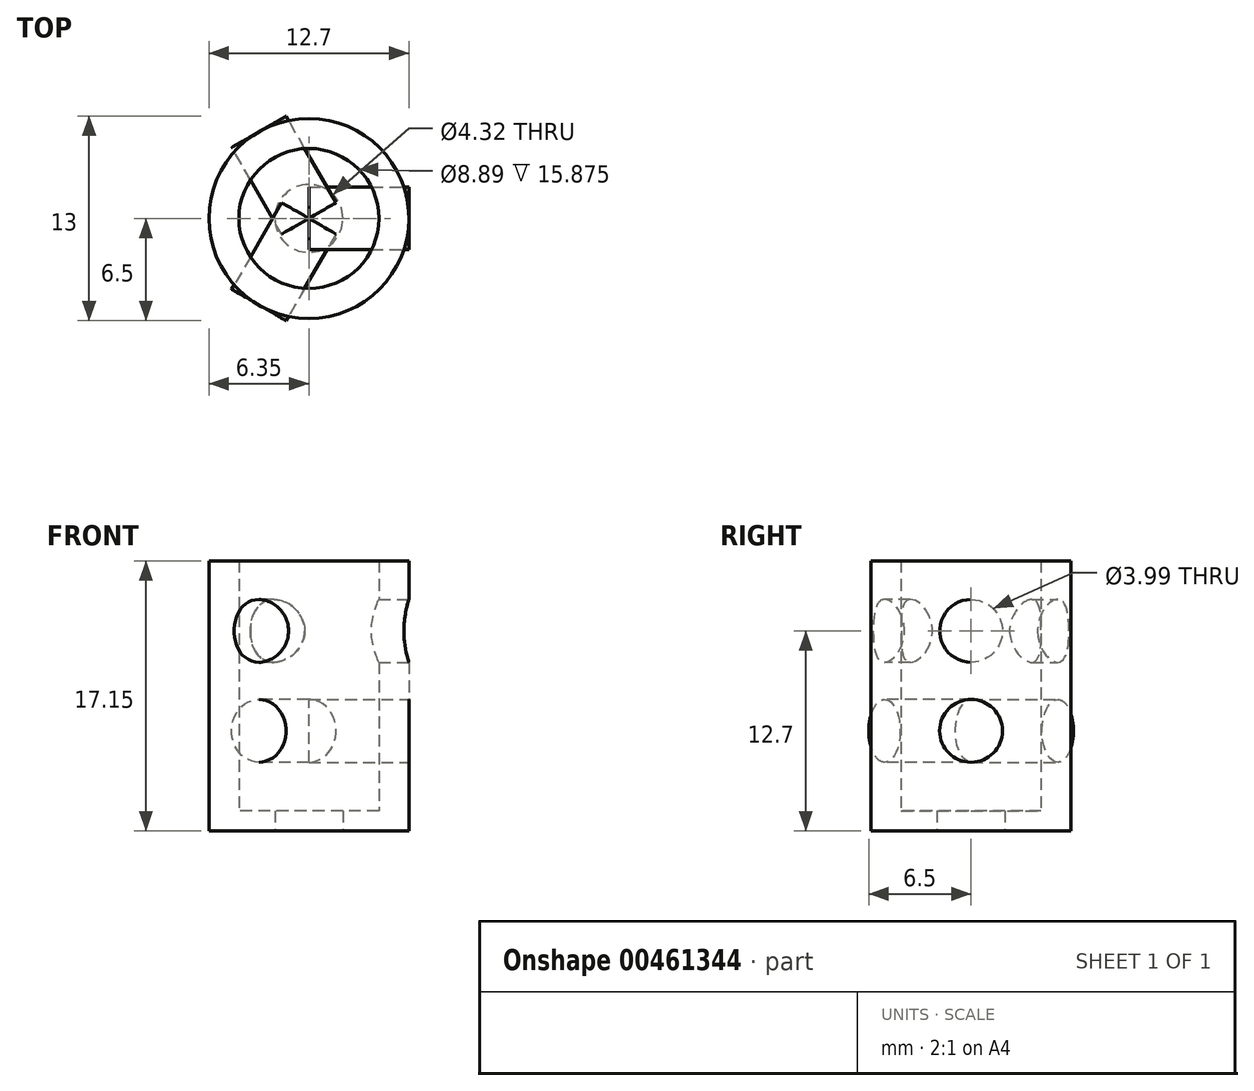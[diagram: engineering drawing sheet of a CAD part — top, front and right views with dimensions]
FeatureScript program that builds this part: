
annotation { "Feature Type Name" : "Feature", "Feature Type Description" : "" }
export const myFeature = defineFeature(function(context is Context, id is Id, definition is map)
    precondition{}
    {
        {
            var Q0;
            Q0=qCreatedBy(makeId("Top.planeOp"),FACE);
            var sketch = newSketch(context, id + "F0", { "sketchPlane" : qUnion([Q0])});
            skCircle(sketch, "E0", {"center": v(0, 0) * mm, "radius": 6.35 * mm});
            skCircle(sketch, "E1", {"center": v(0, 0) * mm, "radius": 2.16 * mm});
            skSolve(sketch);
        }
        {
            var Q0;
            Q0=makeQuery(id+"F0.imprint","IMPRINT",FACE,{"disambiguationData":[TD([[makeQuery(id+"F0.imprint","IMPRINT",EDGE,{"derivedFrom":sQuery(id+"F0.wireOp",EDGE,"E0")}),1.0]])]});
            extrude(context, id + "F1", {"entities" : qUnion([Q0]), "depth" : 1.27 * mm});
        }
        {
            var Q0;
            Q0=makeQuery(id+"F1.opExtrude","CAP_FACE",FACE,{"disambiguationData":[OSD([sQuery(id+"F0.wireOp",EDGE,"E0"),sQuery(id+"F0.wireOp",EDGE,"E1")])],"isStart":false});
            var sketch = newSketch(context, id + "F2", { "sketchPlane" : qUnion([Q0])});
            skCircle(sketch, "E2", {"center": v(0, 0) * mm, "radius": 6.35 * mm});
            skCircle(sketch, "E3", {"center": v(0, 0) * mm, "radius": 4.45 * mm});
            skSolve(sketch);
        }
        {
            var Q0;
            Q0=makeQuery(id+"F2.imprint","IMPRINT",FACE,{"disambiguationData":[TD([[makeQuery(id+"F2.imprint","IMPRINT",EDGE,{"derivedFrom":sQuery(id+"F2.wireOp",EDGE,"E2")}),1.0]])]});
            extrude(context, id + "F3", {"entities" : qUnion([Q0]), "operationType" : NewBodyOperationType.ADD, "depth" : 15.88 * mm, "offsetDistance" : 25.4 * mm});
        }
        {
            var Q0;
            Q0=qCreatedBy(makeId("Right.planeOp"),FACE);
            cPlane(context, id + "F4", {"entities" : qUnion([Q0]), "cplaneType" : CPlaneType.OFFSET, "offset" : 6.35 * mm, "width" : 152.4 * mm, "height" : 152.4 * mm});
        }
        {
            var Q0;
            Q0=qCreatedBy(id+"F4.planeOp",FACE);
            var sketch = newSketch(context, id + "F5", { "sketchPlane" : qUnion([Q0])});
            skCircle(sketch, "E4", {"center": v(0, 6.35) * mm, "radius": 2 * mm});
            skCircle(sketch, "E5", {"center": v(0, 12.7) * mm, "radius": 2 * mm});
            skSolve(sketch);
        }
        {
            var Q0;
            Q0 = qSketchRegion(id + "F5", true);
            extrude(context, id + "F6", {"entities" : qUnion([Q0]), "oppositeDirection" : true, "depth" : 6.35 * mm, "offsetDistance" : 25.4 * mm});
        }
        {
            var Q0;
            Q0=makeQuery(id+"F6.opExtrude","SWEPT_BODY",BODY,{"disambiguationData":[OSD([sQuery(id+"F5.wireOp",EDGE,"E4")])]});
            var Q1;
            Q1=makeQuery(id+"F6.opExtrude","SWEPT_BODY",BODY,{"disambiguationData":[OSD([sQuery(id+"F5.wireOp",EDGE,"E5")])]});
            var Q2;
            Q2=makeQuery(id+"F3.opExtrude","CAP_EDGE",EDGE,{"disambiguationData":[OSD([sQuery(id+"F2.wireOp",EDGE,"E3")])],"isStart":false});
            circularPattern(context, id + "F7", {"entities" : qUnion([Q0, Q1]), "axis" : qUnion([Q2]), "angle" : 360 * degree, "instanceCount" : 3, "equalSpace" : true});
        }
        {
            var Q0;
            Q0=makeQuery(id+"F6.opExtrude","CAP_FACE",FACE,{"disambiguationData":[OSD([sQuery(id+"F5.wireOp",EDGE,"E4")])],"isStart":true});
            var sketch = newSketch(context, id + "F8", { "sketchPlane" : qUnion([Q0])});
            skSolve(sketch);
        }
        {
            var Q0;
            Q0=makeQuery(id+"F8.imprint","IMPRINT",FACE,{"disambiguationData":[TD([[makeQuery(id+"F8.imprint","IMPRINT",EDGE,{"derivedFrom":makeQuery(id+"F6.opExtrude","CAP_EDGE",EDGE,{"disambiguationData":[OSD([sQuery(id+"F5.wireOp",EDGE,"E4")])],"isStart":true})}),1.0]])]});
            var Q1;
            Q1=makeQuery(id+"F6.opExtrude","CAP_FACE",FACE,{"disambiguationData":[OSD([sQuery(id+"F5.wireOp",EDGE,"E5")])],"isStart":true});
            extrude(context, id + "F9", {"entities" : qUnion([Q0, Q1]), "operationType" : NewBodyOperationType.REMOVE, "oppositeDirection" : true, "depth" : 6.35 * mm, "offsetDistance" : 25.4 * mm});
        }
        {
            var Q0;
            Q0=makeQuery(id+"F7.opPattern","COPY",FACE,{"derivedFrom":makeQuery(id+"F6.opExtrude","CAP_FACE",FACE,{"disambiguationData":[OSD([sQuery(id+"F5.wireOp",EDGE,"E4")])],"isStart":true}),"instanceName":"1"});
            var sketch = newSketch(context, id + "F10", { "sketchPlane" : qUnion([Q0])});
            skSolve(sketch);
        }
        {
            var Q0;
            Q0=makeQuery(id+"F10.imprint","IMPRINT",FACE,{"disambiguationData":[TD([[makeQuery(id+"F10.imprint","IMPRINT",EDGE,{"derivedFrom":makeQuery(id+"F7.opPattern","COPY",EDGE,{"derivedFrom":makeQuery(id+"F6.opExtrude","CAP_EDGE",EDGE,{"disambiguationData":[OSD([sQuery(id+"F5.wireOp",EDGE,"E4")])],"isStart":true}),"instanceName":"1"})}),1.0]])]});
            var Q1;
            Q1=makeQuery(id+"F7.opPattern","COPY",FACE,{"derivedFrom":makeQuery(id+"F6.opExtrude","CAP_FACE",FACE,{"disambiguationData":[OSD([sQuery(id+"F5.wireOp",EDGE,"E5")])],"isStart":true}),"instanceName":"1"});
            extrude(context, id + "F11", {"entities" : qUnion([Q0, Q1]), "operationType" : NewBodyOperationType.REMOVE, "oppositeDirection" : true, "depth" : 6.35 * mm, "offsetDistance" : 25.4 * mm});
        }
        {
            var Q0;
            Q0=makeQuery(id+"F7.opPattern","COPY",FACE,{"derivedFrom":makeQuery(id+"F6.opExtrude","CAP_FACE",FACE,{"disambiguationData":[OSD([sQuery(id+"F5.wireOp",EDGE,"E4")])],"isStart":true}),"instanceName":"2"});
            var sketch = newSketch(context, id + "F12", { "sketchPlane" : qUnion([Q0])});
            skSolve(sketch);
        }
        {
            var Q0;
            Q0=makeQuery(id+"F12.imprint","IMPRINT",FACE,{"disambiguationData":[TD([[makeQuery(id+"F12.imprint","IMPRINT",EDGE,{"derivedFrom":makeQuery(id+"F7.opPattern","COPY",EDGE,{"derivedFrom":makeQuery(id+"F6.opExtrude","CAP_EDGE",EDGE,{"disambiguationData":[OSD([sQuery(id+"F5.wireOp",EDGE,"E4")])],"isStart":true}),"instanceName":"2"})}),1.0]])]});
            var Q1;
            Q1=makeQuery(id+"F7.opPattern","COPY",FACE,{"derivedFrom":makeQuery(id+"F6.opExtrude","CAP_FACE",FACE,{"disambiguationData":[OSD([sQuery(id+"F5.wireOp",EDGE,"E5")])],"isStart":true}),"instanceName":"2"});
            extrude(context, id + "F13", {"entities" : qUnion([Q0, Q1]), "operationType" : NewBodyOperationType.REMOVE, "oppositeDirection" : true, "depth" : 6.35 * mm, "offsetDistance" : 25.4 * mm});
        }
    });
